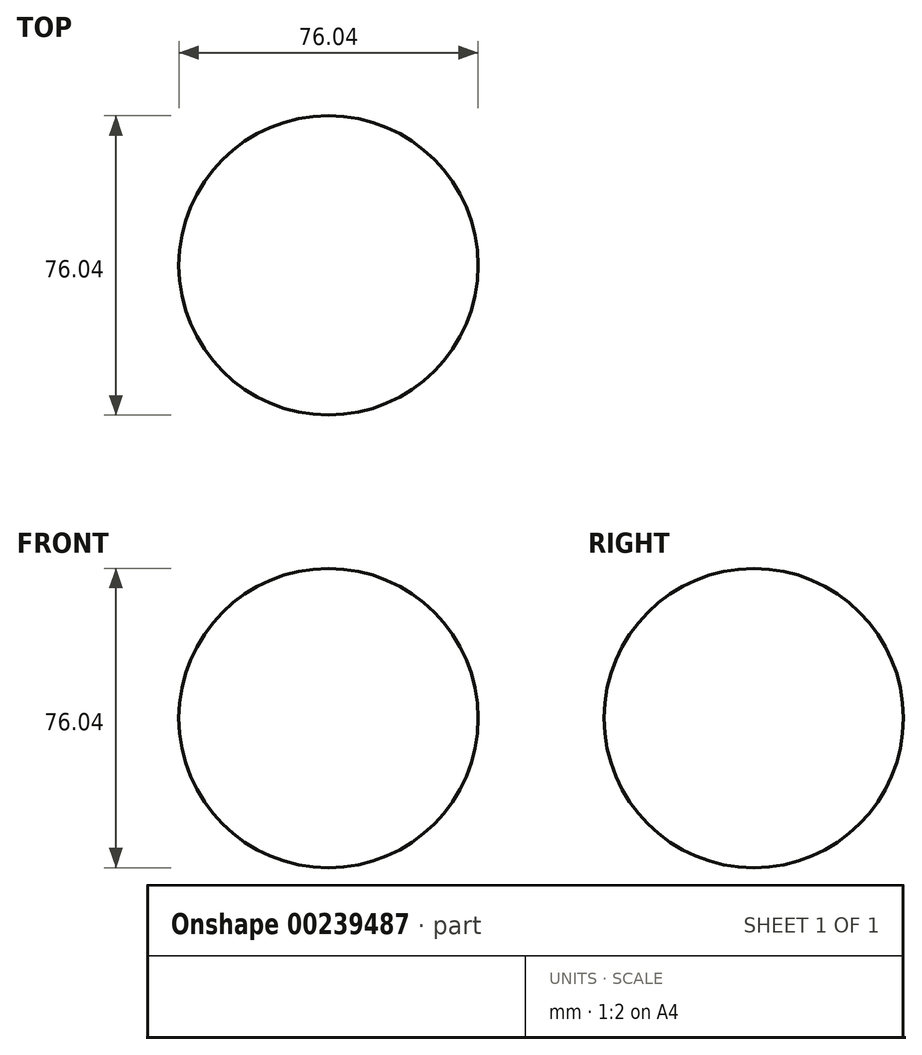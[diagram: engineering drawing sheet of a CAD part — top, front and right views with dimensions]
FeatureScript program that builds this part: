
annotation { "Feature Type Name" : "Feature", "Feature Type Description" : "" }
export const myFeature = defineFeature(function(context is Context, id is Id, definition is map)
    precondition{}
    {
        {
            var Q0;
            Q0=qCreatedBy(makeId("Front.planeOp"),FACE);
            var sketch = newSketch(context, id + "F0", { "sketchPlane" : qUnion([Q0])});
            skArc(sketch, "E0", {"start": v(0, -38.02) * mm, "mid": v(38.02, 0) * mm, "end": v(0, 38.02) * mm});
            skLineSegment(sketch, "E1", {"start": v(0, 38.02) * mm, "end": v(0, -38.02) * mm});
            skSolve(sketch);
        }
        {
            var Q0;
            Q0=makeQuery(id+"F0.imprint","IMPRINT",FACE,{"disambiguationData":[TD([[makeQuery(id+"F0.imprint","IMPRINT",EDGE,{"derivedFrom":sQuery(id+"F0.wireOp",EDGE,"E0")}),1.0]])]});
            var Q1;
            Q1=sQuery(id+"F0.wireOp",EDGE,"E1");
            revolve(context, id + "F1", {"entities" : qUnion([Q0]), "axis" : qUnion([Q1]), "revolveType" : RevolveType.FULL});
        }
    });
